# Revit family: Napkin_Disposal-Bobrick-ConturaSeries-B-4353
name_source: partatom
category: Specialty Equipment
units: mm (PartAtom-declared; Revit-internal decimal feet)

## family parameters
Cut with Voids When Loaded = No
Host = Face
OmniClass Number = 23.40.20.21.24
OmniClass Title = Sanitary Napkin and Tampon Dispensers, Disposal Units
Part Type = Normal
Room Calculation Point = No
Round Connector Dimension = Use Diameter
Shared = Yes

## types (1)
- B4353
    Assembly Code = E1090900
    Default Elevation = 30"
    Description = ConturaSeries® Recessed Sanitary Napkin Disposal with Removable Polyethylene Receptacle
    Finish = Metal-Bobrick-Stainless Steel
    Height = 11"
    Installation Type = Wall Mount
    Length = 5 1/4"
    Manufacturer = Bobrick
    Material = Metal-Bobrick-Stainless Steel
    Model = B-4353
    Price = Prices may vary. Please consult Manufacturer Representative for most up-to-date price list.
    Product Documentation Link = https://www.bobrick.com
    Product Page URL = https://www.bobrick.com
    URL = https://www.bobrick.com
    Warranty Information = 3 Year Limited Warranty
    Width = 12 3/4"

## geometry (parser evidence)
native form markers: Sweep x3
no freeform markers — native parametric forms only
